FCSTD DOCUMENT  (FreeCAD 2023.131R26244 +5365 (Git))
Label: tinyMakeShelves
License: All rights reserved
LicenseURL: http://en.wikipedia.org/wiki/All_rights_reserved
objects: App::Link×17, App::FeaturePython×10, Part::FeaturePython×10
note: 5 computed .brp shape members not serialized (recipe doc carries the construction recipe); baked Part::Feature solids carry a one-line shape summary decoded from their .brp
EXTERNAL_REF file=9100-KEEPOUT/expectations.FCStd obj=Part
EXTERNAL_REF file=9100-KEEPOUT/Workstation-SevilleClassics_AirliftProS3.FCStd obj=Part
EXTERNAL_REF file=9100-KEEPOUT/roadLegalWidth.FCStd obj=Body
EXTERNAL_REF file=9100-KEEPOUT/bedQueen.FCStd obj=Part
EXTERNAL_REF file=9100-KEEPOUT/human.FCStd obj=Part
EXTERNAL_REF file=9100-KEEPOUT/flightDeck-rough.FCStd obj=Assembly002
EXTERNAL_REF file=1110z-Extrusions-Timbers/verticalTimber.FCStd obj=Part
EXTERNAL_REF file=9100-KEEPOUT/workbench.FCStd obj=Part

FEATURE [App::Link] Link  label="expectations-Part"
  AutoLinkLabel = true
  AutoPlacement = true
  LinkedObject = -> <external 9100-KEEPOUT/expectations.FCStd>#Part
  SyncGroupVisibility = false
  TreeRank = 1
  _LinkVersion = 1
FEATURE [App::Link] Link001  label="Workstation-SevilleClassics_AirliftProS3-Part"
  AutoLinkLabel = true
  AutoPlacement = true
  LinkPlacement = pos=(1552,976.001,1381) rot=(-1,0,0;1.5708rad)
  LinkedObject = -> <external 9100-KEEPOUT/Workstation-SevilleClassics_AirliftProS3.FCStd>#Part
  Placement = pos=(1552,976.001,1381) rot=(-1,0,0;1.5708rad)
  SyncGroupVisibility = false
  TreeRank = 2
  _LinkVersion = 1
FEATURE [App::FeaturePython] Constraints  # WARN: FeaturePython — macro-defined, semantics opaque (R4)
  TreeRank = 4
  _LinkVersion = 1
  _Version = 1
FEATURE [App::FeaturePython] Elements  # WARN: FeaturePython — macro-defined, semantics opaque (R4)
  TreeRank = 5
  _LinkVersion = 1
FEATURE [App::Link] Link002  label="roadLegalWidth-Body"
  AutoLinkLabel = false
  AutoPlacement = true
  LinkPlacement = pos=(-38.0001,-0.000369407,2580) rot=(0.57735,0.57735,-0.57735;2.0944rad)
  LinkedObject = -> <external 9100-KEEPOUT/roadLegalWidth.FCStd>#Body
  Placement = pos=(-38.0001,-0.000369407,2580) rot=(0.57735,0.57735,-0.57735;2.0944rad)
  SyncGroupVisibility = false
  TreeRank = 8
  _LinkOwner = 6
  _LinkVersion = 1
FEATURE [App::Link] Link003  label="bedQueen-Part"
  AutoLinkLabel = false
  AutoPlacement = true
  LinkPlacement = pos=(3886,734.999,0.00157614) rot=(0,0.707107,0.707107;3.14159rad)
  LinkedObject = -> <external 9100-KEEPOUT/bedQueen.FCStd>#Part
  Placement = pos=(3886,734.999,0.00157614) rot=(0,0.707107,0.707107;3.14159rad)
  SyncGroupVisibility = false
  TreeRank = 9
  _LinkOwner = 6
  _LinkVersion = 1
FEATURE [App::Link] Link004  label="human-Part"
  AutoLinkLabel = false
  AutoPlacement = true
  LinkPlacement = pos=(1270,9.99906,612) rot=(-1,0,0;1.5708rad)
  LinkedObject = -> <external 9100-KEEPOUT/human.FCStd>#Part
  Placement = pos=(1270,9.99906,612) rot=(-1,0,0;1.5708rad)
  SyncGroupVisibility = false
  TreeRank = 10
  _LinkVersion = 1
FEATURE [App::Link] Link005  label="flightDeck-Assembly"
  AutoLinkLabel = false
  AutoPlacement = true
  LinkPlacement = pos=(1542,514,2164) rot=(-1,0,0;1.5708rad)
  LinkedObject = -> <external 9100-KEEPOUT/flightDeck-rough.FCStd>#Assembly002
  Placement = pos=(1542,514,2164) rot=(-1,0,0;1.5708rad)
  SyncGroupVisibility = false
  TreeRank = 11
  _LinkVersion = 1
FEATURE [App::FeaturePython] Constraints001  # WARN: FeaturePython — macro-defined, semantics opaque (R4)
  TreeRank = 13
  _LinkVersion = 1
  _Version = 1
FEATURE [App::FeaturePython] Elements001  # WARN: FeaturePython — macro-defined, semantics opaque (R4)
  TreeRank = 14
  _LinkVersion = 1
FEATURE [App::FeaturePython] Constraints002  # WARN: FeaturePython — macro-defined, semantics opaque (R4)
  TreeRank = 18
  _LinkVersion = 1
  _Version = 1
FEATURE [App::FeaturePython] Elements002  # WARN: FeaturePython — macro-defined, semantics opaque (R4)
  TreeRank = 19
  _LinkVersion = 1
FEATURE [Part::FeaturePython] Parts002  # WARN: FeaturePython — macro-defined, semantics opaque (R4)
  FixShape = 1
  Group = -> [Link001,Link004,Link005]
  GroupMode = 0
  InvalidShape = false
  TreeRank = 20
  ValidateShape = false
  _LinkVersion = 1
FEATURE [Part::FeaturePython] Assembly002  label="workstation-Assembly"  # WARN: FeaturePython — macro-defined, semantics opaque (R4)
  AutoRelax = true
  BuildShape = 0
  FixShape = 1
  Freeze = false
  Group = -> [Constraints002,Elements002,Parts002]
  InvalidShape = false
  Placement = pos=(-527,0.000442624,3186) rot=(0,1,0;1.5708rad)
  TreeRank = 17
  ValidateShape = false
  Verbose = false
  _LinkVersion = 1
  _SolverType = 1
  _Version = 1
FEATURE [App::FeaturePython] Constraints003  # WARN: FeaturePython — macro-defined, semantics opaque (R4)
  TreeRank = 22
  _LinkVersion = 1
  _Version = 1
FEATURE [App::FeaturePython] Elements003  # WARN: FeaturePython — macro-defined, semantics opaque (R4)
  TreeRank = 23
  _LinkVersion = 1
FEATURE [App::Link] Link006  label="verticalTimber-Part"
  AutoLinkLabel = false
  AutoPlacement = true
  LinkedObject = -> <external 1110z-Extrusions-Timbers/verticalTimber.FCStd>#Part
  SyncGroupVisibility = false
  TreeRank = 25
  _LinkOwner = 22
  _LinkVersion = 1
FEATURE [App::Link] Link007  label="verticalTimber-Part001"
  AutoLinkLabel = false
  AutoPlacement = true
  LinkPlacement = pos=(85.9996,3464,-3.81469e-06) rot=(0,0,1;1.5708rad)
  LinkedObject = -> <external 1110z-Extrusions-Timbers/verticalTimber.FCStd>#Part
  Placement = pos=(85.9996,3464,-3.81469e-06) rot=(0,0,1;1.5708rad)
  SyncGroupVisibility = false
  TreeRank = 26
  _LinkOwner = 22
  _LinkVersion = 1
FEATURE [App::Link] Link008  label="verticalTimber-Part002"
  AutoLinkLabel = false
  AutoPlacement = true
  LinkPlacement = pos=(-3922,-0.999533,0) rot=(0,0,1;0rad)
  LinkedObject = -> <external 1110z-Extrusions-Timbers/verticalTimber.FCStd>#Part
  Placement = pos=(-3922,-0.999533,0) rot=(0,0,1;0rad)
  SyncGroupVisibility = false
  TreeRank = 27
  _LinkOwner = 22
  _LinkVersion = 1
FEATURE [App::Link] Link009  label="verticalTimber-Part003"
  AutoLinkLabel = false
  AutoPlacement = true
  LinkPlacement = pos=(-1213,0.000144601,0) rot=(0,0,1;0rad)
  LinkedObject = -> <external 1110z-Extrusions-Timbers/verticalTimber.FCStd>#Part
  Placement = pos=(-1213,0.000144601,0) rot=(0,0,1;0rad)
  SyncGroupVisibility = false
  TreeRank = 28
  _LinkOwner = 22
  _LinkVersion = 1
FEATURE [App::Link] Link010  label="verticalTimber-Part004"
  AutoLinkLabel = false
  AutoPlacement = true
  LinkPlacement = pos=(-2663,0.000317454,0) rot=(0,0,1;0rad)
  LinkedObject = -> <external 1110z-Extrusions-Timbers/verticalTimber.FCStd>#Part
  Placement = pos=(-2663,0.000317454,0) rot=(0,0,1;0rad)
  SyncGroupVisibility = false
  TreeRank = 29
  _LinkOwner = 22
  _LinkVersion = 1
FEATURE [App::Link] Link011  label="verticalTimber-Part005"
  AutoLinkLabel = false
  AutoPlacement = true
  LinkPlacement = pos=(1.52588e-06,1347,0.000146484) rot=(0,0,1;0rad)
  LinkedObject = -> <external 1110z-Extrusions-Timbers/verticalTimber.FCStd>#Part
  Placement = pos=(1.52588e-06,1347,0.000146484) rot=(0,0,1;0rad)
  SyncGroupVisibility = false
  TreeRank = 30
  _LinkOwner = 22
  _LinkVersion = 1
FEATURE [App::Link] Link012  label="verticalTimber-Part006"
  AutoLinkLabel = false
  AutoPlacement = true
  LinkPlacement = pos=(-3924,1346,0) rot=(0,0,1;0rad)
  LinkedObject = -> <external 1110z-Extrusions-Timbers/verticalTimber.FCStd>#Part
  Placement = pos=(-3924,1346,0) rot=(0,0,1;0rad)
  SyncGroupVisibility = false
  TreeRank = 31
  _LinkOwner = 22
  _LinkVersion = 1
FEATURE [App::Link] Link013  label="verticalTimber-Part007"
  AutoLinkLabel = false
  AutoPlacement = true
  LinkPlacement = pos=(-7.62939e-06,751,0) rot=(0,0,1;0rad)
  LinkedObject = -> <external 1110z-Extrusions-Timbers/verticalTimber.FCStd>#Part
  Placement = pos=(-7.62939e-06,751,0) rot=(0,0,1;0rad)
  SyncGroupVisibility = false
  TreeRank = 32
  _LinkOwner = 22
  _LinkVersion = 1
FEATURE [App::Link] Link014  label="verticalTimber-Part008"
  AutoLinkLabel = false
  AutoPlacement = true
  LinkPlacement = pos=(-3922,753.001,0) rot=(0,0,1;0rad)
  LinkedObject = -> <external 1110z-Extrusions-Timbers/verticalTimber.FCStd>#Part
  Placement = pos=(-3922,753.001,0) rot=(0,0,1;0rad)
  SyncGroupVisibility = false
  TreeRank = 33
  _LinkOwner = 22
  _LinkVersion = 1
FEATURE [App::Link] Link015  label="verticalTimber-Part009"
  AutoLinkLabel = false
  AutoPlacement = true
  LinkPlacement = pos=(-3885,3464,0) rot=(0,0,1;1.5708rad)
  LinkedObject = -> <external 1110z-Extrusions-Timbers/verticalTimber.FCStd>#Part
  Placement = pos=(-3885,3464,0) rot=(0,0,1;1.5708rad)
  SyncGroupVisibility = false
  TreeRank = 34
  _LinkOwner = 22
  _LinkVersion = 1
FEATURE [Part::FeaturePython] Parts003  # WARN: FeaturePython — macro-defined, semantics opaque (R4)
  FixShape = 1
  Group = -> [Link006,Link007,Link008,Link009,Link010,Link011,Link012,Link013,Link014,Link015]
  GroupMode = 0
  InvalidShape = false
  TreeRank = 24
  ValidateShape = false
  _LinkVersion = 1
FEATURE [Part::FeaturePython] Assembly003  label="Frame-verticalTimber-Assembly003"  # WARN: FeaturePython — macro-defined, semantics opaque (R4)
  AutoRelax = true
  BuildShape = 0
  FixShape = 1
  Freeze = false
  Group = -> [Constraints003,Elements003,Parts003]
  InvalidShape = false
  Placement = pos=(89,9.00005,-0.000128388) rot=(0,0.707107,0.707107;3.14159rad)
  TreeRank = 21
  ValidateShape = false
  Verbose = false
  _LinkVersion = 1
  _SolverType = 1
  _Version = 1
FEATURE [App::FeaturePython] Constraints004  # WARN: FeaturePython — macro-defined, semantics opaque (R4)
  TreeRank = 36
  _LinkVersion = 1
  _Version = 1
FEATURE [App::FeaturePython] Elements004  # WARN: FeaturePython — macro-defined, semantics opaque (R4)
  TreeRank = 37
  _LinkVersion = 1
FEATURE [Part::FeaturePython] Parts004  # WARN: FeaturePython — macro-defined, semantics opaque (R4)
  FixShape = 1
  Group = -> [Assembly003]
  GroupMode = 0
  InvalidShape = false
  TreeRank = 38
  ValidateShape = false
  _LinkVersion = 1
FEATURE [Part::FeaturePython] Assembly004  label="Frame"  # WARN: FeaturePython — macro-defined, semantics opaque (R4)
  AutoRelax = true
  BuildShape = 0
  FixShape = 1
  Freeze = false
  Group = -> [Constraints004,Elements004,Parts004]
  InvalidShape = false
  TreeRank = 35
  ValidateShape = false
  Verbose = false
  _LinkVersion = 1
  _SolverType = 1
  _Version = 1
FEATURE [App::Link] Link016  label="workbench-Part"
  AutoLinkLabel = false
  AutoPlacement = true
  LinkPlacement = pos=(957.072,558.802,771.144) rot=(-1,0,0;1.5708rad)
  LinkedObject = -> <external 9100-KEEPOUT/workbench.FCStd>#Part
  Placement = pos=(957.072,558.802,771.144) rot=(-1,0,0;1.5708rad)
  SyncGroupVisibility = false
  TreeRank = 39
  _LinkOwner = 6
  _LinkVersion = 0
FEATURE [Part::FeaturePython] Parts  # WARN: FeaturePython — macro-defined, semantics opaque (R4)
  FixShape = 1
  Group = -> [Link,Link002,Link003,Assembly002,Link016]
  GroupMode = 0
  InvalidShape = false
  TreeRank = 6
  ValidateShape = false
  _LinkVersion = 1
FEATURE [Part::FeaturePython] Assembly  label="KEEPOUT-Assembly"  # WARN: FeaturePython — macro-defined, semantics opaque (R4)
  AutoRelax = true
  BuildShape = 0
  FixShape = 1
  Freeze = false
  Group = -> [Constraints,Elements,Parts]
  InvalidShape = false
  TreeRank = 7
  ValidateShape = false
  Verbose = false
  _LinkVersion = 1
  _SolverType = 1
  _Version = 1
FEATURE [Part::FeaturePython] Parts001  # WARN: FeaturePython — macro-defined, semantics opaque (R4)
  FixShape = 1
  Group = -> [Assembly,Assembly004]
  GroupMode = 0
  InvalidShape = false
  TreeRank = 15
  ValidateShape = false
  _LinkVersion = 1
FEATURE [Part::FeaturePython] Assembly001  label="tinyMakeLab-Assembly"  # WARN: FeaturePython — macro-defined, semantics opaque (R4)
  AutoRelax = true
  BuildShape = 0
  FixShape = 1
  Freeze = false
  Group = -> [Constraints001,Elements001,Parts001]
  InvalidShape = false
  TreeRank = 16
  ValidateShape = false
  Verbose = false
  _LinkVersion = 1
  _SolverType = 1
  _Version = 1

RESOLVED EXTERNAL PARTS (link-assembly join: the EXTERNAL_REF files above that resolve inside this repo's crawl, each included once):
---- part 1110z-Extrusions-Timbers/verticalTimber.FCStd = doc fcstd_4d12ed297985 ----
FCSTD DOCUMENT  (FreeCAD 2023.131R26244 +5365 (Git))
Label: verticalTimber
License: All rights reserved
LicenseURL: http://en.wikipedia.org/wiki/All_rights_reserved
objects: Sketcher::SketchObject×1, PartDesign::Pad×1, PartDesign::Body×1, App::Part×1
note: 6 computed .brp shape members not serialized (recipe doc carries the construction recipe); baked Part::Feature solids carry a one-line shape summary decoded from their .brp

FEATURE [Sketcher::SketchObject] Sketch
  ArcFitTolerance = 1e-06
  AttachmentSupport = -> [XY_Plane]
  ExternalBSplineMaxDegree = 5
  ExternalBSplineTolerance = 0.0001
  FixShape = 1
  FullyConstrained = true
  InternalTolerance = 1e-06
  InvalidShape = false
  MakeInternals = false
  MapMode = 5
  Support = -> [XY_Plane]
  TreeRank = 13
  ValidateShape = false
  sketch-geometry (4):
    g0: LineSegment StartX=0 StartY=0 StartZ=0 EndX=88.9 EndY=0 EndZ=0
    g1: LineSegment StartX=88.9 StartY=0 StartZ=0 EndX=88.9 EndY=38.1 EndZ=0
    g2: LineSegment StartX=88.9 StartY=38.1 StartZ=0 EndX=0 EndY=38.1 EndZ=0
    g3: LineSegment StartX=0 StartY=38.1 StartZ=0 EndX=0 EndY=0 EndZ=0
  constraints (11):
    c: Coincident(g0,g1)
    c: Coincident(g1,g2)
    c: Coincident(g2,g3)
    c: Coincident(g3,g0)
    c: Horizontal(g0)
    c: Horizontal(g2)
    c: Vertical(g1)
    c: Vertical(g3)
    c: Coincident(g0,g-1)
    c: DistanceX(g0,g0) = 88.9
    c: DistanceY(g3,g3) = 38.1
FEATURE [PartDesign::Pad] Pad
  AddSubType = 0
  AlongSketchNormal = false
  AutoTaperInnerAngle = true
  CheckUpToFaceLimits = true
  ClaimChildren = false
  Direction = (0,0,1)
  Fit = 0
  FitJoin = 0
  FixShape = 1
  InnerFit = 0
  InnerFitJoin = 0
  InvalidShape = false
  Length = 2171.7
  Length2 = 100
  Linearize = true
  NewSolid = false
  Profile = -> Sketch
  Suppress = false
  TaperInnerAngle = 0
  TaperInnerAngleRev = 0
  TreeRank = 14
  Type = 0
  ValidateShape = false
  _ProfileBasedVersion = 1
FEATURE [PartDesign::Body] Body
  AutoGroupSolids = false
  ClaimAllChildren = false
  ExportMode = 0
  FixShape = 1
  Group = -> [Sketch,Pad]
  InvalidShape = false
  Origin = -> Origin001
  Tip = -> Pad
  TreeRank = 12
  ValidateShape = false
  _ExportChildren = -> [Pad]
  _GroupVersion = 1
FEATURE [App::Part] Part  label="verticalTimber-Part"
  ClaimAllChildren = false
  ExportMode = 1
  Group = -> [Body]
  Origin = -> Origin
  TreeRank = 1
  _ExportChildren = -> [Body]
  _GroupVersion = 1
---- part 9100-KEEPOUT/Workstation-SevilleClassics_AirliftProS3.FCStd = doc fcstd_cc4e70de0ca7 ----
FCSTD DOCUMENT  (FreeCAD 2023.131R26244 +5365 (Git))
Label: Workstation-SevilleClassics_AirliftProS3
License: All rights reserved
LicenseURL: http://en.wikipedia.org/wiki/All_rights_reserved
objects: PartDesign::Pad×4, Sketcher::SketchObject×2, PartDesign::Body×1, App::Part×1
note: 17 computed .brp shape members not serialized (recipe doc carries the construction recipe); baked Part::Feature solids carry a one-line shape summary decoded from their .brp

FEATURE [Sketcher::SketchObject] Sketch
  ArcFitTolerance = 1e-06
  AttachmentSupport = -> [XY_Plane]
  ExternalBSplineMaxDegree = 5
  ExternalBSplineTolerance = 0.0001
  FixShape = 1
  FullyConstrained = true
  InternalTolerance = 1e-06
  InvalidShape = false
  MakeInternals = false
  MapMode = 5
  Support = -> [XY_Plane]
  TreeRank = 13
  ValidateShape = false
  sketch-geometry (4):
    g0: LineSegment StartX=-1479.55 StartY=0 StartZ=0 EndX=1479.55 EndY=0 EndZ=0
    g1: LineSegment StartX=1479.55 StartY=0 StartZ=0 EndX=1479.55 EndY=762 EndZ=0
    g2: LineSegment StartX=1479.55 StartY=762 StartZ=0 EndX=-1479.55 EndY=762 EndZ=0
    g3: LineSegment StartX=-1479.55 StartY=762 StartZ=0 EndX=-1479.55 EndY=0 EndZ=0
  constraints (11):
    c: Coincident(g0,g1)
    c: Coincident(g1,g2)
    c: Coincident(g2,g3)
    c: Coincident(g3,g0)
    c: Horizontal(g0)
    c: Horizontal(g2)
    c: Vertical(g1)
    c: Vertical(g3)
    c: Symmetric(g0,g0,g-1)
    c: DistanceY(g3,g3) = 762
    c: DistanceX(g0,g0) = 2959.1
FEATURE [PartDesign::Pad] Pad
  AddSubType = 0
  AlongSketchNormal = false
  AutoTaperInnerAngle = true
  CheckUpToFaceLimits = true
  ClaimChildren = false
  Direction = (0,0,1)
  Fit = 0
  FitJoin = 0
  FixShape = 1
  InnerFit = 0
  InnerFitJoin = 0
  InvalidShape = false
  Length = 76.2
  Length2 = 100
  Linearize = true
  NewSolid = false
  Profile = -> Sketch
  Reversed = true
  Suppress = false
  TaperInnerAngle = 0
  TaperInnerAngleRev = 0
  TreeRank = 14
  Type = 0
  ValidateShape = false
  _ProfileBasedVersion = 1
FEATURE [PartDesign::Pad] Pad001
  AddSubType = 0
  AlongSketchNormal = false
  AutoTaperInnerAngle = true
  CheckUpToFaceLimits = true
  ClaimChildren = false
  Direction = (0,0,1)
  Fit = 0
  FitJoin = 0
  FixShape = 1
  InnerFit = 0
  InnerFitJoin = 0
  InvalidShape = false
  Length = 965.2
  Length2 = -76.2
  Linearize = true
  NewSolid = true
  Profile = -> Sketch
  Reversed = true
  Suppress = false
  TaperInnerAngle = 0
  TaperInnerAngleRev = 0
  TreeRank = 15
  Type = 4
  ValidateShape = false
  _ProfileBasedVersion = 1
FEATURE [Sketcher::SketchObject] Sketch001
  ArcFitTolerance = 1e-06
  AttachmentSupport = -> [Sketch]
  ExternalBSplineMaxDegree = 5
  ExternalBSplineTolerance = 0.0001
  ExternalGeometry = -> [Sketch]
  FixShape = 1
  FullyConstrained = false
  InternalTolerance = 1e-06
  InvalidShape = false
  MakeInternals = false
  MapMode = 5
  Support = -> [Sketch]
  TreeRank = 16
  ValidateShape = false
  sketch-geometry (11):
    g0: LineSegment StartX=-723.9 StartY=609.6 StartZ=0 EndX=723.9 EndY=609.6 EndZ=0
    g1: LineSegment StartX=723.9 StartY=609.6 StartZ=0 EndX=1479.56 EndY=-347.179 EndZ=0
    g2: LineSegment StartX=-723.9 StartY=609.6 StartZ=0 EndX=-1479.56 EndY=-347.179 EndZ=0
    g3: LineSegment [constr] StartX=-1479.56 StartY=-347.179 StartZ=0 EndX=1479.56 EndY=-347.179 EndZ=0
    g4: GeomPoint [constr] X=1101.73 Y=131.21 Z=0
    g5: GeomPoint [constr] X=1205.36 Y=0 Z=0
    g6: LineSegment StartX=-1479.56 StartY=-347.179 StartZ=0 EndX=-1513.75 EndY=-347.179 EndZ=0
    g7: LineSegment StartX=-1513.75 StartY=-347.179 StartZ=0 EndX=-741.041 EndY=631.188 EndZ=0
    g8: LineSegment StartX=-741.041 StartY=631.188 StartZ=0 EndX=741.041 EndY=631.188 EndZ=0
    g9: LineSegment StartX=741.041 StartY=631.188 StartZ=0 EndX=1513.75 EndY=-347.179 EndZ=0
    g10: LineSegment StartX=1513.75 StartY=-347.179 StartZ=0 EndX=1479.56 EndY=-347.179 EndZ=0
  constraints (26):
    c: Symmetric(g0,g0,g-2)
    c: DistanceX(g0,g0) = 1447.8
    c: Coincident(g1,g0)
    c: Coincident(g2,g0)
    c: Coincident(g3,g2)
    c: Coincident(g3,g1)
    c: Symmetric(g1,g2,g-2)
    c: Distance(g1) = 1219.2
    c: DistanceY(g0,g-3) = 152.4
    c: Symmetric(g1,g1,g4)
    c: PointOnObject(g5,g1)
    c: PointOnObject(g5,g-1)
    c: Distance(g5,g4) = 167.198
    c: DistanceX(g2,g-3) = 0.01
    c: Coincident(g6,g2)
    c: PointOnObject(g6,g3)
    c: Coincident(g7,g6)
    c: Coincident(g8,g7)
    c: Horizontal(g8)
    c: Coincident(g9,g8)
    c: PointOnObject(g9,g3)
    c: Coincident(g10,g9)
    c: Coincident(g10,g1)
    c: Equal(g6,g10)
    c: Equal(g7,g9)
    c: Parallel(g9,g1)
FEATURE [PartDesign::Pad] Pad002
  AddSubType = 0
  AlongSketchNormal = false
  AutoTaperInnerAngle = true
  CheckUpToFaceLimits = true
  ClaimChildren = false
  Direction = (0,0,1)
  Fit = 0
  FitJoin = 0
  FixShape = 1
  InnerFit = 0
  InnerFitJoin = 0
  InvalidShape = false
  Length = 965.2
  Length2 = 100
  Linearize = true
  NewSolid = true
  Profile = -> Sketch001
  Suppress = false
  TaperInnerAngle = 0
  TaperInnerAngleRev = 0
  TreeRank = 17
  Type = 0
  ValidateShape = false
  _ProfileBasedVersion = 1
FEATURE [PartDesign::Pad] Pad003
  AddSubType = 0
  AlongSketchNormal = false
  AutoTaperInnerAngle = true
  CheckUpToFaceLimits = true
  ClaimChildren = false
  Direction = (0,0,1)
  Fit = 0
  FitJoin = 0
  FixShape = 1
  InnerFit = 0
  InnerFitJoin = 0
  InvalidShape = false
  Length = 609.6
  Length2 = -76.2
  Linearize = true
  NewSolid = true
  Profile = -> Sketch
  Reversed = true
  Suppress = false
  TaperInnerAngle = 0
  TaperInnerAngleRev = 0
  TreeRank = 18
  Type = 4
  ValidateShape = false
  _ProfileBasedVersion = 1
FEATURE [PartDesign::Body] Body
  AutoGroupSolids = false
  ClaimAllChildren = false
  ExportMode = 0
  FixShape = 1
  Group = -> [Sketch,Pad,Pad001,Sketch001,Pad002,Pad003]
  InvalidShape = false
  Origin = -> Origin001
  Tip = -> Pad003
  TreeRank = 12
  ValidateShape = false
  _ExportChildren = -> [Pad,Pad001,Pad002,Pad003]
  _GroupVersion = 1
FEATURE [App::Part] Part  label="Workstation-SevilleClassics_AirliftProS3-Part"
  ClaimAllChildren = false
  ExportMode = 1
  Group = -> [Body]
  Origin = -> Origin
  TreeRank = 1
  _ExportChildren = -> [Body]
  _GroupVersion = 1
---- part 9100-KEEPOUT/bedQueen.FCStd = doc fcstd_6cf1a7897a54 ----
FCSTD DOCUMENT  (FreeCAD 2023.131R26244 +5365 (Git))
Label: bedQueen
License: All rights reserved
LicenseURL: http://en.wikipedia.org/wiki/All_rights_reserved
objects: PartDesign::Pad×2, Sketcher::SketchObject×1, PartDesign::Body×1, App::Part×1
note: 9 computed .brp shape members not serialized (recipe doc carries the construction recipe); baked Part::Feature solids carry a one-line shape summary decoded from their .brp

FEATURE [Sketcher::SketchObject] Sketch
  ArcFitTolerance = 1e-06
  AttachmentSupport = -> [XY_Plane]
  ExternalBSplineMaxDegree = 5
  ExternalBSplineTolerance = 0.0001
  FixShape = 1
  FullyConstrained = true
  InternalTolerance = 1e-06
  InvalidShape = false
  MakeInternals = false
  MapMode = 5
  Support = -> [XY_Plane]
  TreeRank = 10
  ValidateShape = false
  sketch-geometry (4):
    g0: LineSegment StartX=0 StartY=0 StartZ=0 EndX=1524 EndY=0 EndZ=0
    g1: LineSegment StartX=1524 StartY=0 StartZ=0 EndX=1524 EndY=2032 EndZ=0
    g2: LineSegment StartX=1524 StartY=2032 StartZ=0 EndX=0 EndY=2032 EndZ=0
    g3: LineSegment StartX=0 StartY=2032 StartZ=0 EndX=0 EndY=0 EndZ=0
  constraints (11):
    c: Coincident(g0,g1)
    c: Coincident(g1,g2)
    c: Coincident(g2,g3)
    c: Coincident(g3,g0)
    c: Horizontal(g0)
    c: Horizontal(g2)
    c: Vertical(g1)
    c: Vertical(g3)
    c: Coincident(g0,g-1)
    c: DistanceX(g0,g0) = 1524
    c: DistanceY(g3,g3) = 2032
FEATURE [PartDesign::Pad] Pad
  AddSubType = 0
  AlongSketchNormal = false
  AutoTaperInnerAngle = true
  CheckUpToFaceLimits = true
  ClaimChildren = false
  Direction = (0,0,1)
  Fit = 0
  FitJoin = 0
  FixShape = 1
  InnerFit = 0
  InnerFitJoin = 0
  InvalidShape = false
  Length = 215.9
  Length2 = 100
  Linearize = true
  NewSolid = false
  Profile = -> Sketch
  Reversed = true
  Suppress = false
  TaperInnerAngle = 0
  TaperInnerAngleRev = 0
  TreeRank = 11
  Type = 0
  ValidateShape = false
  _ProfileBasedVersion = 1
FEATURE [PartDesign::Pad] Pad001
  AddSubType = 0
  AlongSketchNormal = false
  AutoTaperInnerAngle = true
  CheckUpToFaceLimits = true
  ClaimChildren = false
  Direction = (0,0,1)
  Fit = 0
  FitJoin = 0
  FixShape = 1
  InnerFit = 0
  InnerFitJoin = 0
  InvalidShape = false
  Length = 812.8
  Length2 = 100
  Linearize = true
  NewSolid = true
  Profile = -> Sketch
  Suppress = false
  TaperInnerAngle = 0
  TaperInnerAngleRev = 0
  TreeRank = 12
  Type = 0
  ValidateShape = false
  _ProfileBasedVersion = 1
FEATURE [PartDesign::Body] Body  label="bedQueen-Body"
  AutoGroupSolids = false
  ClaimAllChildren = false
  ExportMode = 0
  FixShape = 1
  Group = -> [Sketch,Pad,Pad001]
  InvalidShape = false
  Origin = -> Origin
  Tip = -> Pad001
  TreeRank = 9
  ValidateShape = false
  _ExportChildren = -> [Pad,Pad001]
  _GroupVersion = 1
FEATURE [App::Part] Part  label="bedQueen-Part"
  ClaimAllChildren = false
  ExportMode = 1
  Group = -> [Body]
  Origin = -> Origin001
  TreeRank = 15
  _ExportChildren = -> [Body]
  _GroupVersion = 1
---- part 9100-KEEPOUT/expectations.FCStd = doc fcstd_54343b56371e ----
FCSTD DOCUMENT  (FreeCAD 2023.131R26244 +5365 (Git))
Label: expectations
License: All rights reserved
LicenseURL: http://en.wikipedia.org/wiki/All_rights_reserved
objects: Sketcher::SketchObject×3, PartDesign::Pad×3, PartDesign::Body×1, App::Part×1
note: 16 computed .brp shape members not serialized (recipe doc carries the construction recipe); baked Part::Feature solids carry a one-line shape summary decoded from their .brp

FEATURE [Sketcher::SketchObject] Sketch
  ArcFitTolerance = 1e-06
  ExternalBSplineMaxDegree = 5
  ExternalBSplineTolerance = 0.0001
  FixShape = 1
  FullyConstrained = true
  InternalTolerance = 1e-06
  InvalidShape = false
  MakeInternals = false
  MapMode = 2
  TreeRank = 5
  ValidateShape = false
  sketch-geometry (6):
    g0: LineSegment StartX=0 StartY=0 StartZ=0 EndX=0 EndY=2235.2 EndZ=0
    g1: LineSegment StartX=0 StartY=2235.2 StartZ=0 EndX=685.8 EndY=2921 EndZ=0
    g2: LineSegment StartX=685.8 StartY=2921 StartZ=0 EndX=3606.8 EndY=2921 EndZ=0
    g3: LineSegment StartX=3606.8 StartY=2921 StartZ=0 EndX=4013.2 EndY=2514.6 EndZ=0
    g4: LineSegment StartX=4013.2 StartY=2514.6 StartZ=0 EndX=4013.2 EndY=0 EndZ=0
    g5: LineSegment StartX=4013.2 StartY=0 StartZ=0 EndX=0 EndY=0 EndZ=0
  constraints (17):
    c: Coincident(g0,g-1)
    c: Vertical(g0)
    c: Coincident(g1,g0)
    c: Coincident(g2,g1)
    c: Horizontal(g2)
    c: Coincident(g3,g2)
    c: Coincident(g4,g3)
    c: PointOnObject(g4,g-1)
    c: Vertical(g4)
    c: Coincident(g5,g4)
    c: Coincident(g5,g0)
    c: DistanceY(g0,g1) = 2921
    c: DistanceX(g5,g5) = 4013.2
    c: DistanceY(g0,g0) = 2235.2
    c: DistanceY(g4,g3) = 2514.6
    c: Angle(g0,g1) = 2.35619
    c: Angle(g3,g4) = 2.35619
FEATURE [PartDesign::Pad] Pad
  AddSubType = 0
  AlongSketchNormal = false
  AutoTaperInnerAngle = true
  CheckUpToFaceLimits = true
  ClaimChildren = false
  Direction = (0,0,1)
  Fit = 0
  FitJoin = 0
  FixShape = 1
  InnerFit = 0
  InnerFitJoin = 0
  InvalidShape = false
  Length = 10
  Length2 = 100
  Linearize = true
  NewSolid = false
  Profile = -> Sketch
  Reversed = true
  Suppress = false
  TaperInnerAngle = 0
  TaperInnerAngleRev = 0
  TreeRank = 16
  Type = 0
  ValidateShape = false
  _ProfileBasedVersion = 1
FEATURE [Sketcher::SketchObject] Sketch001
  ArcFitTolerance = 1e-06
  AttachmentSupport = -> [XZ_Plane]
  ExternalBSplineMaxDegree = 5
  ExternalBSplineTolerance = 0.0001
  ExternalGeometry = -> [Pad]
  FixShape = 1
  FullyConstrained = true
  InternalTolerance = 1e-06
  InvalidShape = false
  MakeInternals = false
  MapMode = 5
  Placement = pos=(0,0,0) rot=(1,0,0;1.5708rad)
  Support = -> [XZ_Plane]
  TreeRank = 17
  ValidateShape = false
  sketch-geometry (4):
    g0: LineSegment StartX=0 StartY=0 StartZ=0 EndX=4013.2 EndY=0 EndZ=0
    g1: LineSegment StartX=4013.2 StartY=0 StartZ=0 EndX=4013.2 EndY=3556 EndZ=0
    g2: LineSegment StartX=4013.2 StartY=3556 StartZ=0 EndX=0 EndY=3556 EndZ=0
    g3: LineSegment StartX=0 StartY=3556 StartZ=0 EndX=0 EndY=0 EndZ=0
  constraints (11):
    c: Coincident(g0,g1)
    c: Coincident(g1,g2)
    c: Coincident(g2,g3)
    c: Coincident(g3,g0)
    c: Horizontal(g0)
    c: Horizontal(g2)
    c: Vertical(g1)
    c: Vertical(g3)
    c: Coincident(g0,g-1)
    c: PointOnObject(g-3,g1)
    c: DistanceY(g3,g3) = 3556
FEATURE [PartDesign::Pad] Pad001
  AddSubType = 0
  AlongSketchNormal = false
  AutoTaperInnerAngle = true
  BaseFeature = -> Pad
  CheckUpToFaceLimits = true
  ClaimChildren = false
  Direction = (0,-1,-2e-16)
  Fit = 0
  FitJoin = 0
  FixShape = 1
  InnerFit = 0
  InnerFitJoin = 0
  InvalidShape = false
  Length = 10
  Length2 = 100
  Linearize = true
  NewSolid = false
  Profile = -> Sketch001
  Reversed = true
  Suppress = false
  TaperInnerAngle = 0
  TaperInnerAngleRev = 0
  TreeRank = 18
  Type = 0
  ValidateShape = false
  _ProfileBasedVersion = 1
FEATURE [Sketcher::SketchObject] Sketch002
  ArcFitTolerance = 1e-06
  AttachmentSupport = -> [Pad001]
  ExternalBSplineMaxDegree = 5
  ExternalBSplineTolerance = 0.0001
  FixShape = 1
  FullyConstrained = true
  InternalTolerance = 1e-06
  InvalidShape = false
  MakeInternals = false
  MapMode = 5
  Placement = pos=(4013.2,0,0) rot=(0.57735,0.57735,0.57735;2.0944rad)
  Support = -> [Pad001]
  TreeRank = 19
  ValidateShape = false
  sketch-geometry (5):
    g0: LineSegment StartX=0 StartY=1422.4 StartZ=0 EndX=2057.4 EndY=1422.4 EndZ=0
    g1: LineSegment StartX=2057.4 StartY=1422.4 StartZ=0 EndX=2057.4 EndY=3289.3 EndZ=0
    g2: LineSegment StartX=2057.4 StartY=3289.3 StartZ=0 EndX=0 EndY=3289.3 EndZ=0
    g3: LineSegment StartX=0 StartY=3289.3 StartZ=0 EndX=0 EndY=1422.4 EndZ=0
    g4: LineSegment [constr] StartX=0 StartY=-1.8e-15 StartZ=0 EndX=0 EndY=1422.4 EndZ=0
  constraints (14):
    c: Coincident(g0,g1)
    c: Coincident(g1,g2)
    c: Coincident(g2,g3)
    c: Coincident(g3,g0)
    c: Horizontal(g0)
    c: Horizontal(g2)
    c: Vertical(g1)
    c: Vertical(g3)
    c: Coincident(g4,g-1)
    c: Coincident(g4,g0)
    c: DistanceY(g4,g4) = 1422.4
    c: DistanceY(g3,g3) = 1866.9
    c: DistanceX(g0,g0) = 2057.4
    c: Vertical(g4)
FEATURE [PartDesign::Pad] Pad002
  AddSubType = 0
  AlongSketchNormal = false
  AutoTaperInnerAngle = true
  BaseFeature = -> Pad001
  CheckUpToFaceLimits = true
  ClaimChildren = false
  Direction = (1,0,0)
  Fit = 0
  FitJoin = 0
  FixShape = 1
  InnerFit = 0
  InnerFitJoin = 0
  InvalidShape = false
  Length = 10
  Length2 = 100
  Linearize = true
  NewSolid = false
  Profile = -> Sketch002
  Suppress = false
  TaperInnerAngle = 0
  TaperInnerAngleRev = 0
  TreeRank = 20
  Type = 0
  ValidateShape = false
  _ProfileBasedVersion = 1
FEATURE [PartDesign::Body] Body
  AutoGroupSolids = false
  ClaimAllChildren = false
  ExportMode = 0
  FixShape = 1
  Group = -> [Sketch,Pad,Sketch001,Pad001,Sketch002,Pad002]
  InvalidShape = false
  Origin = -> Origin001
  Tip = -> Pad002
  TreeRank = 15
  ValidateShape = false
  _ExportChildren = -> [Pad,Pad001,Pad002]
  _GroupVersion = 1
FEATURE [App::Part] Part  label="expectations-Part"
  ClaimAllChildren = false
  ExportMode = 1
  Group = -> [Body]
  Origin = -> Origin
  TreeRank = 4
  _ExportChildren = -> [Body]
  _GroupVersion = 1
---- part 9100-KEEPOUT/flightDeck-rough.FCStd = doc fcstd_d2cc3164dc83 (54364 chars; too large to inline — full recipe in that document) ----
---- part 9100-KEEPOUT/human.FCStd = doc fcstd_0a822c1981e3 ----
FCSTD DOCUMENT  (FreeCAD 2023.131R26244 +5365 (Git))
Label: human
License: All rights reserved
LicenseURL: http://en.wikipedia.org/wiki/All_rights_reserved
objects: Sketcher::SketchObject×1, PartDesign::Pad×1, PartDesign::Body×1, App::Part×1
note: 6 computed .brp shape members not serialized (recipe doc carries the construction recipe); baked Part::Feature solids carry a one-line shape summary decoded from their .brp

FEATURE [Sketcher::SketchObject] Sketch
  ArcFitTolerance = 1e-06
  AttachmentSupport = -> [XY_Plane]
  ExternalBSplineMaxDegree = 5
  ExternalBSplineTolerance = 0.0001
  FixShape = 1
  FullyConstrained = true
  InternalTolerance = 1e-06
  InvalidShape = false
  MakeInternals = false
  MapMode = 5
  Support = -> [XY_Plane]
  TreeRank = 13
  ValidateShape = false
  sketch-geometry (4):
    g0: LineSegment StartX=0 StartY=0 StartZ=0 EndX=609.6 EndY=0 EndZ=0
    g1: LineSegment StartX=609.6 StartY=0 StartZ=0 EndX=609.6 EndY=609.6 EndZ=0
    g2: LineSegment StartX=609.6 StartY=609.6 StartZ=0 EndX=0 EndY=609.6 EndZ=0
    g3: LineSegment StartX=0 StartY=609.6 StartZ=0 EndX=0 EndY=0 EndZ=0
  constraints (11):
    c: Coincident(g0,g1)
    c: Coincident(g1,g2)
    c: Coincident(g2,g3)
    c: Coincident(g3,g0)
    c: Horizontal(g0)
    c: Horizontal(g2)
    c: Vertical(g1)
    c: Vertical(g3)
    c: Coincident(g0,g-1)
    c: DistanceX(g0,g0) = 609.6
    c: DistanceY(g3,g3) = 609.6
FEATURE [PartDesign::Pad] Pad
  AddSubType = 0
  AlongSketchNormal = false
  AutoTaperInnerAngle = true
  CheckUpToFaceLimits = true
  ClaimChildren = false
  Direction = (0,0,1)
  Fit = 0
  FitJoin = 0
  FixShape = 1
  InnerFit = 0
  InnerFitJoin = 0
  InvalidShape = false
  Length = 1727.2
  Length2 = 100
  Linearize = true
  NewSolid = false
  Profile = -> Sketch
  Suppress = false
  TaperInnerAngle = 0
  TaperInnerAngleRev = 0
  TreeRank = 14
  Type = 0
  ValidateShape = false
  _ProfileBasedVersion = 1
FEATURE [PartDesign::Body] Body
  AutoGroupSolids = false
  ClaimAllChildren = false
  ExportMode = 0
  FixShape = 1
  Group = -> [Sketch,Pad]
  InvalidShape = false
  Origin = -> Origin001
  Tip = -> Pad
  TreeRank = 12
  ValidateShape = false
  _ExportChildren = -> [Pad]
  _GroupVersion = 1
FEATURE [App::Part] Part  label="human-Part"
  ClaimAllChildren = false
  ExportMode = 1
  Group = -> [Body]
  Origin = -> Origin
  TreeRank = 1
  _ExportChildren = -> [Body]
  _GroupVersion = 1
---- part 9100-KEEPOUT/roadLegalWidth.FCStd = doc fcstd_64bc31b5f5f2 ----
FCSTD DOCUMENT  (FreeCAD 2023.131R26244 +5365 (Git))
Label: roadLegalWidth
License: All rights reserved
LicenseURL: http://en.wikipedia.org/wiki/All_rights_reserved
objects: Sketcher::SketchObject×1, PartDesign::Pad×1, PartDesign::Body×1, App::Part×1
note: 6 computed .brp shape members not serialized (recipe doc carries the construction recipe); baked Part::Feature solids carry a one-line shape summary decoded from their .brp

FEATURE [Sketcher::SketchObject] Sketch
  ArcFitTolerance = 1e-06
  AttachmentSupport = -> [XY_Plane]
  ExternalBSplineMaxDegree = 5
  ExternalBSplineTolerance = 0.0001
  FullyConstrained = true
  InternalTolerance = 1e-06
  InvalidShape = false
  MakeInternals = false
  MapMode = 5
  Support = -> [XY_Plane]
  TreeRank = 10
  ValidateShape = true
  sketch-geometry (4):
    g0: LineSegment StartX=0 StartY=0 StartZ=0 EndX=2590.8 EndY=0 EndZ=0
    g1: LineSegment StartX=2590.8 StartY=0 StartZ=0 EndX=2590.8 EndY=12192 EndZ=0
    g2: LineSegment StartX=2590.8 StartY=12192 StartZ=0 EndX=0 EndY=12192 EndZ=0
    g3: LineSegment StartX=0 StartY=12192 StartZ=0 EndX=0 EndY=0 EndZ=0
  constraints (11):
    c: Coincident(g0,g1)
    c: Coincident(g1,g2)
    c: Coincident(g2,g3)
    c: Coincident(g3,g0)
    c: Horizontal(g0)
    c: Horizontal(g2)
    c: Vertical(g1)
    c: Vertical(g3)
    c: Coincident(g0,g-1)
    c: DistanceX(g0,g0) = 2590.8
    c: DistanceY(g3,g3) = 12192
FEATURE [PartDesign::Pad] Pad
  AddSubType = 0
  AlongSketchNormal = false
  AutoTaperInnerAngle = true
  CheckUpToFaceLimits = true
  ClaimChildren = false
  Direction = (0,0,1)
  Fit = 0
  FitJoin = 0
  FixShape = 1
  InnerFit = 0
  InnerFitJoin = 0
  InvalidShape = false
  Length = 10
  Length2 = 100
  Linearize = true
  NewSolid = false
  Profile = -> Sketch
  Reversed = true
  Suppress = false
  TaperInnerAngle = 0
  TaperInnerAngleRev = 0
  TreeRank = 11
  Type = 0
  ValidateShape = false
  _ProfileBasedVersion = 1
FEATURE [PartDesign::Body] Body  label="roadLegalWidth-Body"
  AutoGroupSolids = false
  ClaimAllChildren = false
  ExportMode = 0
  Group = -> [Sketch,Pad]
  InvalidShape = false
  Origin = -> Origin
  Tip = -> Pad
  TreeRank = 9
  ValidateShape = true
  _ExportChildren = -> [Pad]
  _GroupVersion = 1
FEATURE [App::Part] Part  label="roadLegalWidth-Part"
  ClaimAllChildren = false
  ExportMode = 1
  Group = -> [Body]
  Origin = -> Origin001
  TreeRank = 14
  _ExportChildren = -> [Body]
  _GroupVersion = 1
---- part 9100-KEEPOUT/workbench.FCStd = doc fcstd_394ed3991a0b ----
FCSTD DOCUMENT  (FreeCAD 2023.131R26244 +5365 (Git))
Label: workbench
License: All rights reserved
LicenseURL: http://en.wikipedia.org/wiki/All_rights_reserved
objects: PartDesign::Pad×2, Sketcher::SketchObject×1, PartDesign::Body×1, App::Part×1
note: 9 computed .brp shape members not serialized (recipe doc carries the construction recipe); baked Part::Feature solids carry a one-line shape summary decoded from their .brp

FEATURE [Sketcher::SketchObject] Sketch
  ArcFitTolerance = 1e-06
  AttachmentSupport = -> [XY_Plane]
  ExternalBSplineMaxDegree = 5
  ExternalBSplineTolerance = 0.0001
  FixShape = 1
  FullyConstrained = true
  InternalTolerance = 1e-06
  InvalidShape = false
  MakeInternals = false
  MapMode = 5
  Support = -> [XY_Plane]
  TreeRank = 13
  ValidateShape = false
  sketch-geometry (4):
    g0: LineSegment StartX=0 StartY=0 StartZ=0 EndX=1219.2 EndY=0 EndZ=0
    g1: LineSegment StartX=1219.2 StartY=0 StartZ=0 EndX=1219.2 EndY=609.6 EndZ=0
    g2: LineSegment StartX=1219.2 StartY=609.6 StartZ=0 EndX=0 EndY=609.6 EndZ=0
    g3: LineSegment StartX=0 StartY=609.6 StartZ=0 EndX=0 EndY=0 EndZ=0
  constraints (11):
    c: Coincident(g0,g1)
    c: Coincident(g1,g2)
    c: Coincident(g2,g3)
    c: Coincident(g3,g0)
    c: Horizontal(g0)
    c: Horizontal(g2)
    c: Vertical(g1)
    c: Vertical(g3)
    c: Coincident(g0,g-1)
    c: DistanceX(g0,g0) = 1219.2
    c: DistanceY(g3,g3) = 609.6
FEATURE [PartDesign::Pad] Pad
  AddSubType = 0
  AlongSketchNormal = false
  AutoTaperInnerAngle = true
  CheckUpToFaceLimits = true
  ClaimChildren = false
  Direction = (0,0,1)
  Fit = 0
  FitJoin = 0
  FixShape = 1
  InnerFit = 0
  InnerFitJoin = 0
  InvalidShape = false
  Length = 63.5
  Length2 = 100
  Linearize = true
  NewSolid = false
  Profile = -> Sketch
  Suppress = false
  TaperInnerAngle = 0
  TaperInnerAngleRev = 0
  TreeRank = 14
  Type = 0
  ValidateShape = false
  _ProfileBasedVersion = 1
FEATURE [PartDesign::Pad] Pad001
  AddSubType = 0
  AlongSketchNormal = false
  AutoTaperInnerAngle = true
  BaseFeature = -> Pad
  CheckUpToFaceLimits = true
  ClaimChildren = false
  Direction = (0,0,1)
  Fit = 0
  FitJoin = 0
  FixShape = 1
  InnerFit = 0
  InnerFitJoin = 0
  InvalidShape = false
  Length = 546.1
  Length2 = 100
  Linearize = true
  NewSolid = false
  Profile = -> Sketch
  Reversed = true
  Suppress = false
  TaperInnerAngle = 0
  TaperInnerAngleRev = 0
  TreeRank = 15
  Type = 0
  ValidateShape = false
  _ProfileBasedVersion = 1
FEATURE [PartDesign::Body] Body
  AutoGroupSolids = false
  ClaimAllChildren = false
  ExportMode = 0
  FixShape = 1
  Group = -> [Sketch,Pad,Pad001]
  InvalidShape = false
  Origin = -> Origin001
  Tip = -> Pad001
  TreeRank = 12
  ValidateShape = false
  _ExportChildren = -> [Pad,Pad001]
  _GroupVersion = 1
FEATURE [App::Part] Part  label="workbench-Part"
  ClaimAllChildren = false
  ExportMode = 1
  Group = -> [Body]
  Origin = -> Origin
  TreeRank = 1
  _ExportChildren = -> [Body]
  _GroupVersion = 1
